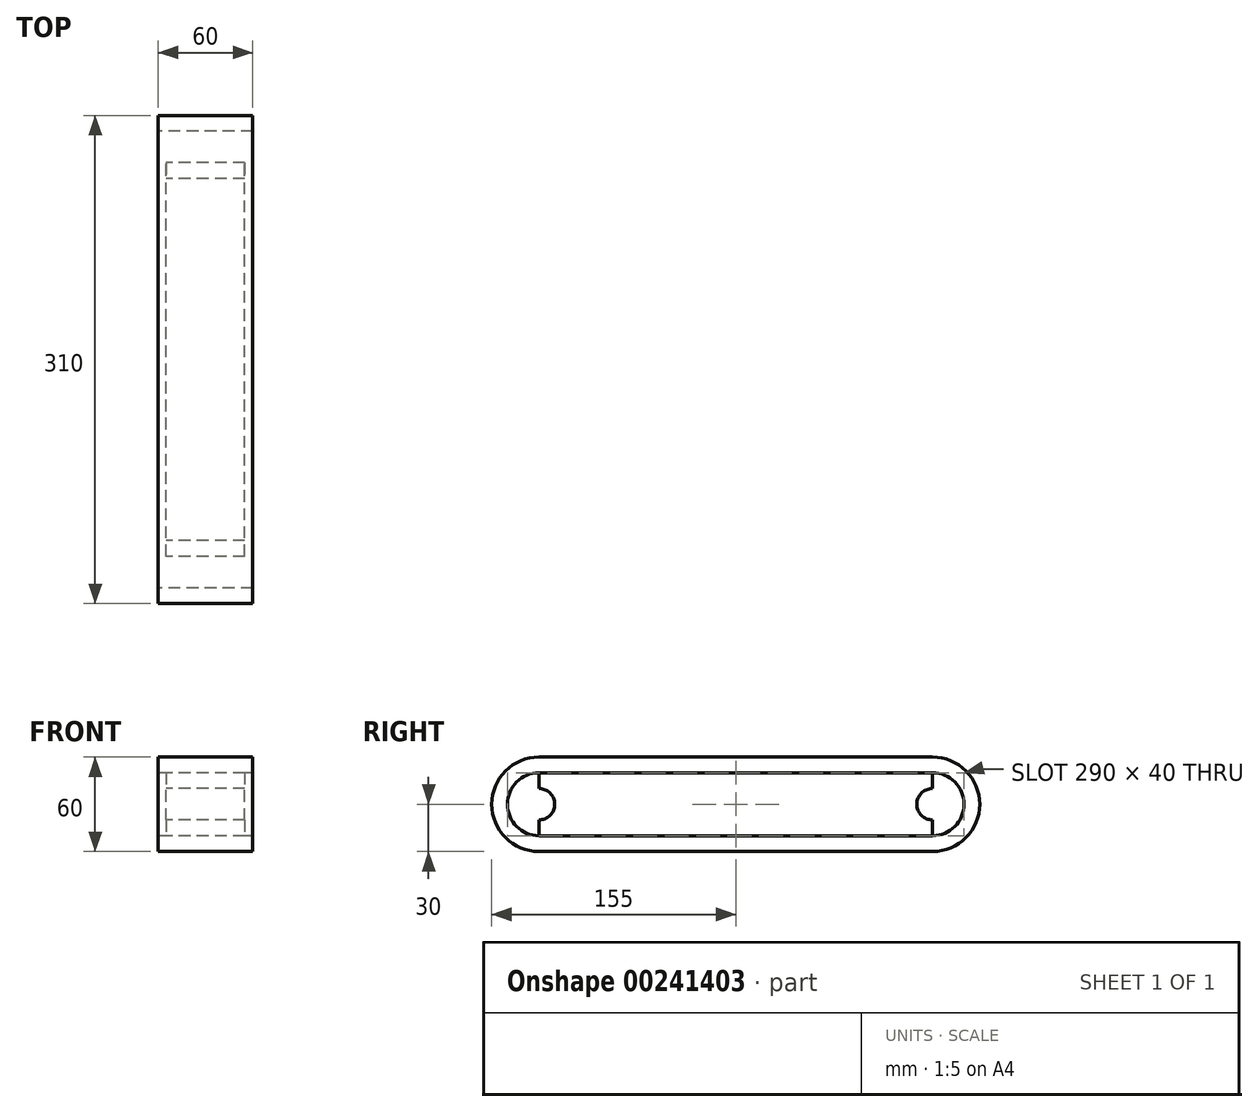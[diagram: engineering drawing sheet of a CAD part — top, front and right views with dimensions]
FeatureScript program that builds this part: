
annotation { "Feature Type Name" : "Feature", "Feature Type Description" : "" }
export const myFeature = defineFeature(function(context is Context, id is Id, definition is map)
    precondition{}
    {
        {
            var Q0;
            Q0=qCreatedBy(makeId("Right.planeOp"),FACE);
            var sketch = newSketch(context, id + "F0", { "sketchPlane" : qUnion([Q0])});
            skLineSegment(sketch, "E0.bottom", {"start": v(-125, 30) * mm, "end": v(125, 30) * mm});
            skLineSegment(sketch, "E0.top", {"start": v(-125, -30) * mm, "end": v(125, -30) * mm});
            skLineSegment(sketch, "E0.left", {"start": v(-125, 30) * mm, "end": v(-125, -30) * mm});
            skLineSegment(sketch, "E0.right", {"start": v(125, 30) * mm, "end": v(125, -30) * mm});
            skPoint(sketch, "E0.middle", {"position": v(0, 0) * mm});
            skLineSegment(sketch, "E1.bottom", {"start": v(-125, 20) * mm, "end": v(125, 20) * mm});
            skLineSegment(sketch, "E1.top", {"start": v(-125, -20) * mm, "end": v(125, -20) * mm});
            skLineSegment(sketch, "E1.left", {"start": v(-125, 20) * mm, "end": v(-125, -20) * mm});
            skLineSegment(sketch, "E1.right", {"start": v(125, 20) * mm, "end": v(125, -20) * mm});
            skArc(sketch, "E2", {"start": v(-125, 30) * mm, "mid": v(-155, 0) * mm, "end": v(-125, -30) * mm});
            skArc(sketch, "E3", {"start": v(125, -30) * mm, "mid": v(155, 0) * mm, "end": v(125, 30) * mm});
            skArc(sketch, "E4", {"start": v(125, -20) * mm, "mid": v(145, 0) * mm, "end": v(125, 20) * mm});
            skArc(sketch, "E5", {"start": v(-125, 20) * mm, "mid": v(-145, 0) * mm, "end": v(-125, -20) * mm});
            skSolve(sketch);
        }
        {
            var Q0;
            Q0=qSketchRegion(id+"F0",true);
            extrude(context, id + "F1", {"entities" : qUnion([Q0]), "depth" : 60 * mm});
        }
        {
            var Q0;
            Q0=makeQuery(id+"F0.imprint","IMPRINT",FACE,{"disambiguationData":[TD([[makeQuery(id+"F0.imprint","IMPRINT",EDGE,{"derivedFrom":sQuery(id+"F0.wireOp",EDGE,"E1.bottom")}),-1.0]])]});
            var Q1;
            Q1=makeQuery(id+"F0.imprint","IMPRINT",FACE,{"disambiguationData":[TD([[makeQuery(id+"F0.imprint","IMPRINT",EDGE,{"derivedFrom":sQuery(id+"F0.wireOp",EDGE,"E1.right")}),1.0]])]});
            var Q2;
            Q2=makeQuery(id+"F0.imprint","IMPRINT",FACE,{"disambiguationData":[TD([[makeQuery(id+"F0.imprint","IMPRINT",EDGE,{"derivedFrom":sQuery(id+"F0.wireOp",EDGE,"E1.left")}),-1.0]])]});
            extrude(context, id + "F2", {"entities" : qUnion([Q0, Q1, Q2]), "operationType" : NewBodyOperationType.ADD, "depth" : 55 * mm, "hasSecondDirection" : true, "secondDirectionOppositeDirection" : true, "secondDirectionDepth" : -5 * mm});
        }
        {
            var Q0;
            Q0=qCreatedBy(makeId("Right.planeOp"),FACE);
            var sketch = newSketch(context, id + "F3", { "sketchPlane" : qUnion([Q0])});
            skCircle(sketch, "E6", {"center": v(-125, 0) * mm, "radius": 10 * mm});
            skCircle(sketch, "E7", {"center": v(125, 0) * mm, "radius": 10 * mm});
            skSolve(sketch);
        }
        {
            var Q0;
            Q0=qSketchRegion(id+"F3",true);
            extrude(context, id + "F4", {"entities" : qUnion([Q0]), "operationType" : NewBodyOperationType.REMOVE, "endBound" : BoundingType.THROUGH_ALL, "depth" : 25 * mm});
        }
    });
